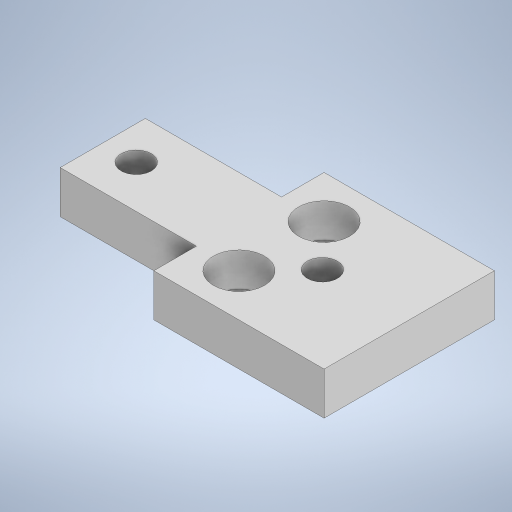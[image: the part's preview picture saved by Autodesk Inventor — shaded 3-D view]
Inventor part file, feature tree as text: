
AUTODESK INVENTOR PART (.ipt)
format: ipt  version: 2024.2 (Build 282272000, 272)  size: 265,728 bytes
history: native  units: in
note: dims shown in document units (in); Inventor stores cm internally (conversion verified against a paired STEP export)
features: sketch x3, extrude x3, projected_geometry x1
ambient origin geometry x8: Origin, YZ Plane, XZ Plane, XY Plane, X Axis, Y Axis, Z Axis, Center Point
bodies: Solid1 (feature_tree)
feature tree (7):
  sketch  "Sketch1"  dims[d0=1.0in d1=1.0in]
  extrude  "Extrusion1"  Depth=1.0in
  extrude  "Extrusion2"  Depth=0.25in
  extrude  "Extrusion3"  Depth=0.5in
  sketch  "Sketch2"  dims[d2=0.25in d3=0.25in]
  projected_geometry  "Projected Loop1"
  sketch  "Sketch3"  dims[d4=0.5in d5=0.49in d6=0.1772in d7=0.1772in d8=0.1772in d9=0.25in d10=0.0in d11=1.1033in d12=0.1772in d13=0.8in d14=0.25in d15=0.0in d16=0.3in d17=0.3in d18=0.2in d19=0.0in d20=0.1772in d21=0.5in d22=0.0344in d23=0.5in d24=0.0344in]
